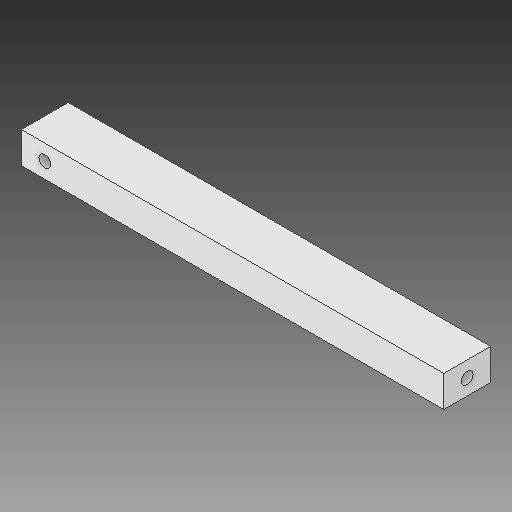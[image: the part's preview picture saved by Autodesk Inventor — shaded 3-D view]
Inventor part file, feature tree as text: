
AUTODESK INVENTOR PART (.ipt)
format: ipt  version: 2017 (Build 210142000, 142)  size: 105,472 bytes
history: native  units: in
note: dims shown in document units (in); Inventor stores cm internally (conversion verified against a paired STEP export)
features: extrude x3, sketch x3
ambient origin geometry x8: Origin, YZ Plane, XZ Plane, XY Plane, X Axis, Y Axis, Z Axis, Center Point
bodies: Solid1 (feature_tree)
feature tree (6):
  extrude  "Extrusion1"  Depth=0.75in
  extrude  "Extrusion2"  Depth=0.5in
  extrude  "Extrusion3"  Depth=0.5in
  sketch  "Sketch1"  dims[d0=6.75in d1=0.75in]
  sketch  "Sketch2"  dims[d2=0.5in d3=0.0in d4=0.1875in]
  sketch  "Sketch3"  dims[d5=0.5in d6=0.0in d7=0.375in d8=0.1875in d9=0.5in d10=0.0in]
